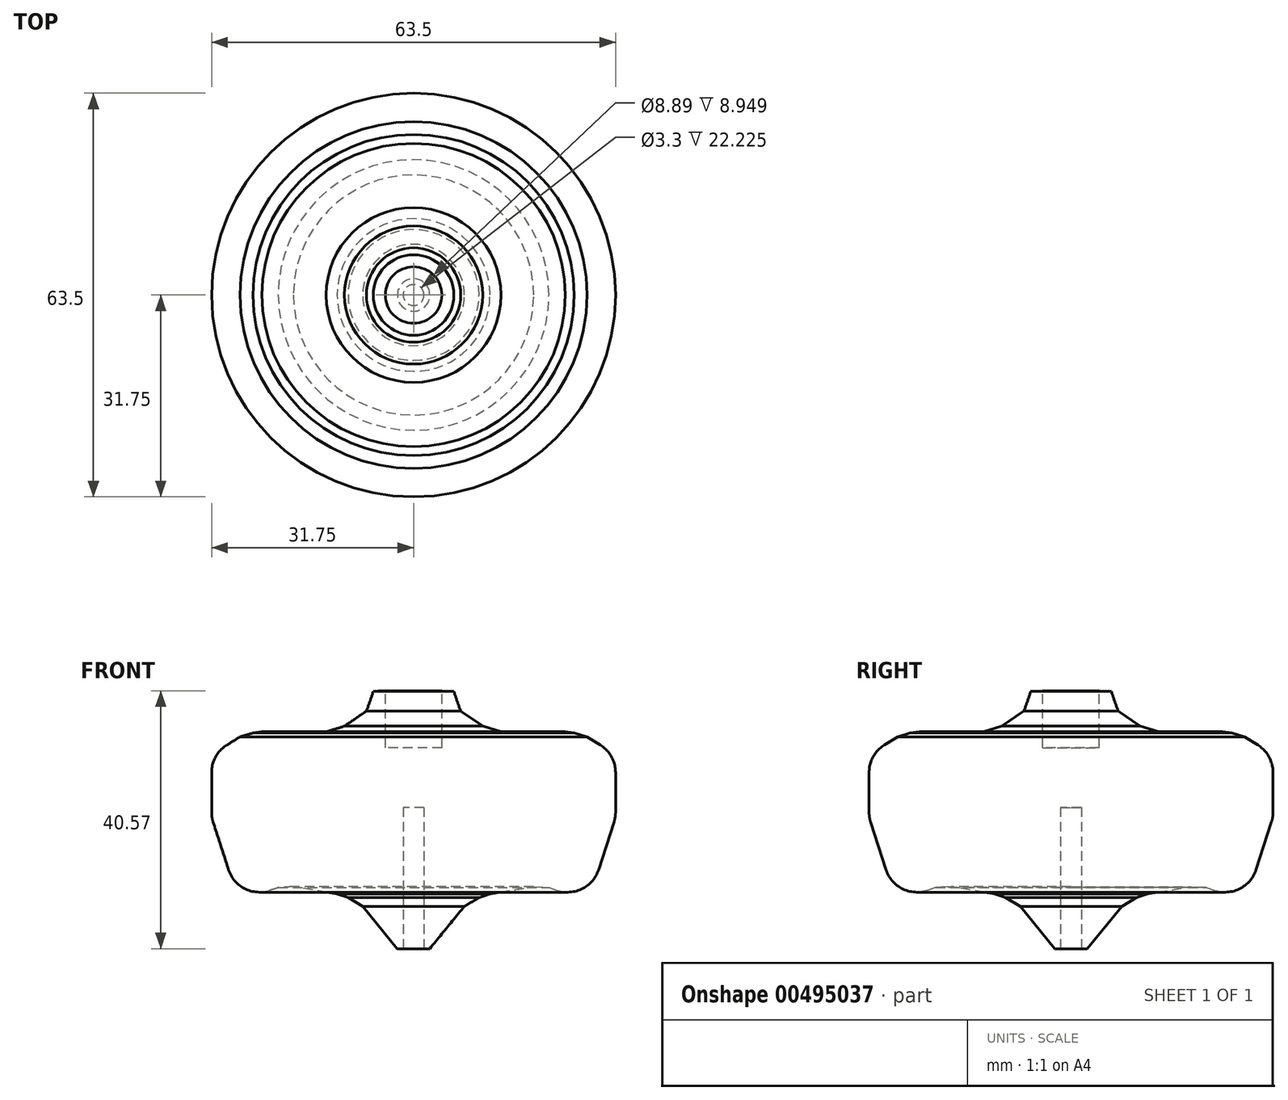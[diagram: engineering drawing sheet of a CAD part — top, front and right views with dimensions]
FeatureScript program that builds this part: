
annotation { "Feature Type Name" : "Feature", "Feature Type Description" : "" }
export const myFeature = defineFeature(function(context is Context, id is Id, definition is map)
    precondition{}
    {
        {
            var Q0;
            Q0=qCreatedBy(makeId("Front.planeOp"),FACE);
            var sketch = newSketch(context, id + "F0", { "sketchPlane" : qUnion([Q0])});
            skLineSegment(sketch, "E0", {"start": v(0, 40.78) * mm, "end": v(0, 0) * mm});
            skArc(sketch, "E1", {"start": v(6.34, 40.48) * mm, "mid": v(7.47, 37.26) * mm, "end": v(8.82, 34.12) * mm});
            skPoint(sketch, "E2.end.orphan", {"position": v(18.48, 17.31) * mm});
            skPoint(sketch, "E3", {"position": v(27.95, 21.42) * mm});
            skLineSegment(sketch, "E4", {"start": v(0, 0) * mm, "end": v(2.55, 0) * mm});
            skLineSegment(sketch, "E5", {"start": v(2.55, 0) * mm, "end": v(9.2, 8.16) * mm});
            skPoint(sketch, "E6.center.orphan", {"position": v(25.93, 21.42) * mm});
            skLineSegment(sketch, "E7", {"start": v(6.34, 40.48) * mm, "end": v(0, 40.78) * mm});
            skLineSegment(sketch, "E8", {"start": v(26.03, 34.12) * mm, "end": v(20.12, 34.12) * mm});
            skLineSegment(sketch, "E9", {"start": v(8.82, 34.12) * mm, "end": v(20.13, 34.12) * mm});
            skPoint(sketch, "E9.startSnap0", {"position": v(23.08, 34.12) * mm});
            skPoint(sketch, "E10.endSnap0", {"position": v(14.59, 9.98) * mm});
            skLineSegment(sketch, "E11", {"start": v(20.1, 9.98) * mm, "end": v(27.53, 7.58) * mm});
            skLineSegment(sketch, "E12", {"start": v(31.75, 20.67) * mm, "end": v(31.75, 30.52) * mm});
            skLineSegment(sketch, "E13", {"start": v(26.03, 34.12) * mm, "end": v(31.75, 30.52) * mm});
            skLineSegment(sketch, "E14", {"start": v(27.53, 7.58) * mm, "end": v(31.75, 20.67) * mm});
            skPoint(sketch, "E15.1.internal.orphan", {"position": v(13.86, 24) * mm});
            skPoint(sketch, "E16.end.orphan", {"position": v(20.13, 24) * mm});
            skPoint(sketch, "E17.start.orphan", {"position": v(30.48, 20.67) * mm});
            skPoint(sketch, "E18.end.orphan", {"position": v(30.48, 13.56) * mm});
            skPoint(sketch, "E19.orphan", {"position": v(19.98, 12.01) * mm});
            skPoint(sketch, "E20.end.orphan", {"position": v(18.48, 14.32) * mm});
            skLineSegment(sketch, "E21", {"start": v(9.2, 8.16) * mm, "end": v(20.1, 9.98) * mm});
            skSolve(sketch);
        }
        {
            var Q0;
            Q0=qSketchRegion(id+"F0",true);
            var Q1;
            Q1=sQuery(id+"F0.wireOp",EDGE,"E0");
            revolve(context, id + "F1", {"entities" : qUnion([Q0]), "axis" : qUnion([Q1]), "revolveType" : RevolveType.FULL});
        }
        {
            var Q0;
            Q0=qCreatedBy(makeId("Top.planeOp"),FACE);
            cPlane(context, id + "F2", {"entities" : qUnion([Q0]), "cplaneType" : CPlaneType.OFFSET, "offset" : 41.15 * mm, "width" : 152.4 * mm, "height" : 152.4 * mm});
        }
        {
            var Q0;
            Q0=qCreatedBy(id+"F2.planeOp",FACE);
            var sketch = newSketch(context, id + "F3", { "sketchPlane" : qUnion([Q0])});
            skCircle(sketch, "E22", {"center": v(0, 0) * mm, "radius": 4.45 * mm});
            skSolve(sketch);
        }
        {
            var Q0;
            Q0=qSketchRegion(id+"F3",true);
            extrude(context, id + "F4", {"entities" : qUnion([Q0]), "operationType" : NewBodyOperationType.REMOVE, "oppositeDirection" : true, "depth" : 9.52 * mm});
        }
        {
            var Q0;
            Q0=qCreatedBy(makeId("Top.planeOp"),FACE);
            var sketch = newSketch(context, id + "F5", { "sketchPlane" : qUnion([Q0])});
            skCircle(sketch, "E23", {"center": v(0, 0) * mm, "radius": 1.65 * mm});
            skSolve(sketch);
        }
        {
            var Q0;
            Q0=makeQuery(id+"F5.imprint","IMPRINT",FACE,{"disambiguationData":[TD([[makeQuery(id+"F5.imprint","IMPRINT",EDGE,{"derivedFrom":sQuery(id+"F5.wireOp",EDGE,"E23")}),1.0]])]});
            extrude(context, id + "F6", {"entities" : qUnion([Q0]), "operationType" : NewBodyOperationType.REMOVE, "depth" : 22.22 * mm});
        }
        {
            var Q0;
            Q0=makeQuery(id+"F1.opRevolve","SWEPT_FACE",FACE,{"disambiguationData":[OSD([sQuery(id+"F0.wireOp",EDGE,"E8"),sQuery(id+"F0.wireOp",EDGE,"E9")])]});
            chamfer(context, id + "F7", {"entities" : qUnion([Q0]), "width" : 5.08 * mm, "tangentPropagation" : true});
        }
        {
            var Q0;
            Q0=makeQuery(id+"F1.opRevolve","SWEPT_FACE",FACE,{"disambiguationData":[OSD([sQuery(id+"F0.wireOp",EDGE,"E12")])]});
            fillet(context, id + "F8", {"entities" : qUnion([Q0]), "radius" : 5.08 * mm, "tangentPropagation" : true, "allowEdgeOverflow" : false});
        }
        {
            var Q0;
            Q0=makeQuery(id+"F1.opRevolve","SWEPT_FACE",FACE,{"disambiguationData":[OSD([sQuery(id+"F0.wireOp",EDGE,"E14")])]});
            fillet(context, id + "F9", {"entities" : qUnion([Q0]), "radius" : 5.08 * mm, "tangentPropagation" : true, "allowEdgeOverflow" : false});
        }
        {
            var Q0;
            Q0=makeQuery(id+"F1.opRevolve","SWEPT_FACE",FACE,{"disambiguationData":[OSD([sQuery(id+"F0.wireOp",EDGE,"E8"),sQuery(id+"F0.wireOp",EDGE,"E9")])]});
            chamfer(context, id + "F10", {"entities" : qUnion([Q0]), "width" : 5.08 * mm, "tangentPropagation" : true});
        }
        {
            var Q0;
            Q0=makeQuery(id+"F1.opRevolve","SWEPT_FACE",FACE,{"disambiguationData":[OSD([sQuery(id+"F0.wireOp",EDGE,"E21")])]});
            chamfer(context, id + "F11", {"entities" : qUnion([Q0]), "width" : 5.08 * mm, "tangentPropagation" : true});
        }
        {
            var Q0;
            {var subQ0=sQuery(id+"F0.wireOp",EDGE,"E21");Q0=makeQuery(id+"F11.opChamfer","BLEND_EDGE",EDGE,{"blendedFrom":[makeQuery(id+"F1.opRevolve","SWEPT_EDGE",EDGE,{"disambiguationData":[OSD([sQuery(id+"F0.wireOp",EDGE,"E5"),subQ0])]}),makeQuery(id+"F1.opRevolve","SWEPT_FACE",FACE,{"disambiguationData":[OSD([subQ0])]})],"blendedInto":[makeQuery(id+"F1.opRevolve","SWEPT_FACE",FACE,{"disambiguationData":[OSD([subQ0])]})]});}
            chamfer(context, id + "F12", {"entities" : qUnion([Q0]), "width" : 5.08 * mm, "tangentPropagation" : true});
        }
    });
